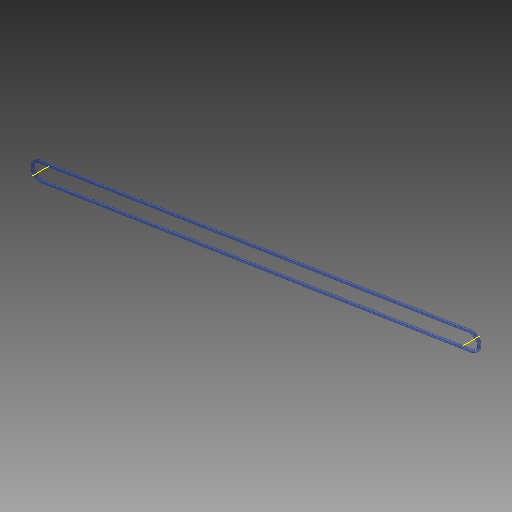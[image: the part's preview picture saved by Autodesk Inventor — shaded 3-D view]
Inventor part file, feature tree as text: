
AUTODESK INVENTOR PART (.ipt)
format: ipt  version: 2017 (Build 210142000, 142)  size: 135,168 bytes
history: native  units: mm
features: other x5, plane x2, pattern_linear x1
ambient origin geometry x8: Origin, YZ Plane, XZ Plane, XY Plane, X Axis, Y Axis, Z Axis, Center Point
bodies: Solid1 (feature_tree), Solid (feature_tree)
feature tree (8):
  other  "Work Axis1"
  other  "Work Axis2"
  plane  "Work Plane2"
  plane  "Work Plane3"
  other  "Path"
  other  "Section Plane"
  pattern_linear  "Strand Pattern"  Spacing1=0.0mm  [1 undecoded]
  other  "Section Sketch"
note: 1 required parameter value undecoded (feature->parameter linkage not recoverable at this tier; creation-order binding heuristic only, values carry confidence <= 0.55)
